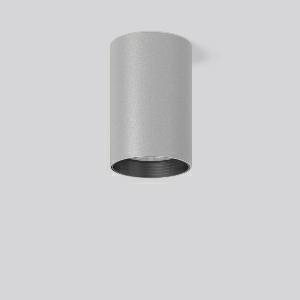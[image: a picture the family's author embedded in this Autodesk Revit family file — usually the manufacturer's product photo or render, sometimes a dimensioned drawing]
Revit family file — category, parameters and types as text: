
# Revit family: heledon_maxi_a_931243_004_9efc
name_source: partatom
category: Lighting Fixtures
units: mm (PartAtom-declared; Revit-internal decimal feet)

## family parameters
Cut with Voids When Loaded = No
Host = Face
Light Source = No
Part Type = Normal
Room Calculation Point = No
Round Connector Dimension = Use Diameter
Shared = No

## types (1)
- HELEDON maxi A (1 x LED Modul 920 meat+, 1900 lm, 2000)
    Apparent Load = 33 VA
    Approval mark = CE
    CIE Flux Codes = 96 99 100 100 100
    Color Rendering = 90
    Color Temperature = 2000
    Default Elevation = 1800 mm
    Description = Series: HELEDON maxi
Cylindrical surface-mounted downlight. Housing: die-cast aluminium, powder-coated. Internal ceiling frame polycarbonate with bayonet mounting. Black plastic ring and recessed LED to prevent glare from the side. Optical assembly with lens made of plastic (polycarbonate) for the best homogeneous light distribution - can be changed without tools. Special LED for illumination of meat included. Suitable for Ceiling mounting. Easy installation with a separate ceiling frame with bayonet mounting and plug connection. Driver integrated. Connected via plug-in connector. High quality converter without flickering and stroboscopic effect. The following accessories can be mounted without use of tools: interchangeable lenses, decorative glasses, honeycomb louvre, clear and frosted diffusers, white interchangeable plastic ring. 
Colour: silver
Diameter: 123 mm
Height: 183 mm
Lamp: LED
Socket: without socket
Colour temperature: meat +
System power: 33 W
Rated luminous flux: 1900 lm
Luminous efficiency: 58 lm/W
Control gear: Regulated power supply
Protection class: I
Type of protection: IP 20
    Height = 183 mm
    Lamp = 1 x LED Modul 920 meat+
    Lamp Light Flux = 1900 lm
    Lamp count = 1
    Length = 123 mm
    Lifetime = 50000 h
    Luminous efficacy = 58 lm/W
    Manufacturer = RZB
    ModVariant = No
    Model = 931243.004
    Mounting Place = Ceiling
    Mounting Type = Surface mounted
    Number of Poles = 1
    OnlyDefault = Yes
    Power Factor = 1
    Product Name = HELEDON maxi A
    Product group = Surface mounted downlights
    ProductGroupID = 302
    Protection Class = Protection class I
    Protection Degree = IP 20
    RLX_Detail_Level = 1
    RLX_Emergency_Light_Flux = 0 lm
    RLX_Emergency_Type = 0
    RLX_Emergency_Type_DB = No
    RlxData = <blob elided: 96345 chars, md5=93a19c98>
    Socket = socket
    Standby Power = 0 W
    System Light Flux = 1900 lm
    System Power = 33 W
    Type Comments = Product without accessories
    Type Image = 931193.004.jpg
    URL = http://relux.com
    VarID = ---
    Voltage = 230 V
    Voltage Range = 220-240 V
    Weight = 0.00 kg
    Width = 0 mm  [stored 0 ft]

note: [stored X ft] marks values corroborated as IEEE doubles in the binary element streams (Revit-internal decimal feet)

## geometry (parser evidence)
native form markers: Blend x4, Sweep x10
no freeform markers — native parametric forms only
